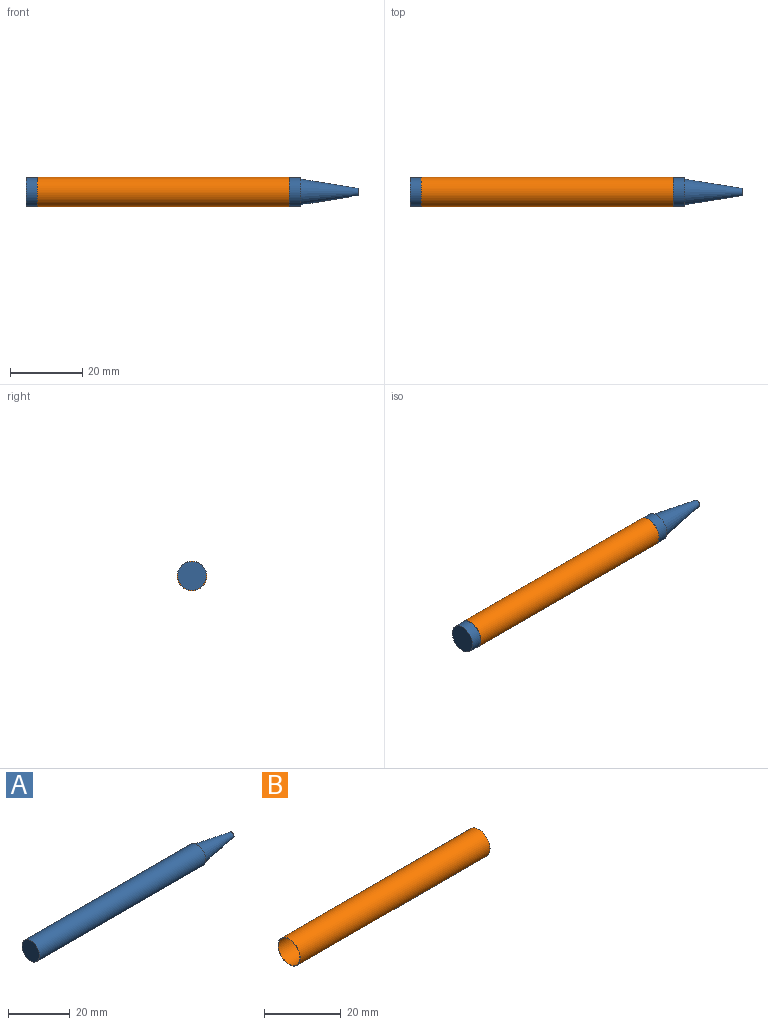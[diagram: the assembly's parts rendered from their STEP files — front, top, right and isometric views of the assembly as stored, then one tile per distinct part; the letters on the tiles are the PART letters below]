
ASSEMBLY  parts=2 mates=1
PART A: 5 faces, bbox 92.1x7.9x7.9 mm
  f0: cylinder r=3.97mm len=76.2mm, axis (-1,0,0), area 1900.2mm2, adj f1,f2
  f1: plane 7.94x7.94mm, normal (1,0,0), area 9.5mm2, adj f0,f4
  f2: plane 7.94x7.94mm, normal (-1,0,0), area 49.5mm2, adj f0
  f3: plane 1.98x1.98mm, normal (1,0,0), area 3.1mm2, adj f4
  f4: cone r=0.99mm half-angle=9.2deg, axis (-1,0,0), area 230.4mm2, adj f1,f3
PART B: 4 faces, bbox 69.9x8.2x8.2 mm
  f0: cylinder r=4.09mm len=69.85mm, axis (-1,0,0), area 1796.7mm2, adj f1,f2
  f1: plane 8.19x8.19mm, normal (1,0,0), area 3.2mm2, adj f0,f3
  f2: plane 8.19x8.19mm, normal (-1,0,0), area 3.2mm2, adj f0,f3
  f3: cylinder r=3.97mm len=69.85mm, axis (1,0,0), area 1741.8mm2, adj f1,f2
PLACE A t=(-15.33,13.37,-6.54)mm
PLACE B t=(-12.15,13.37,-6.54)mm
MATE fastened B.f0 <-> A.f0  axis (-1,0,0) through (22.77,13.37,-6.54)mm
